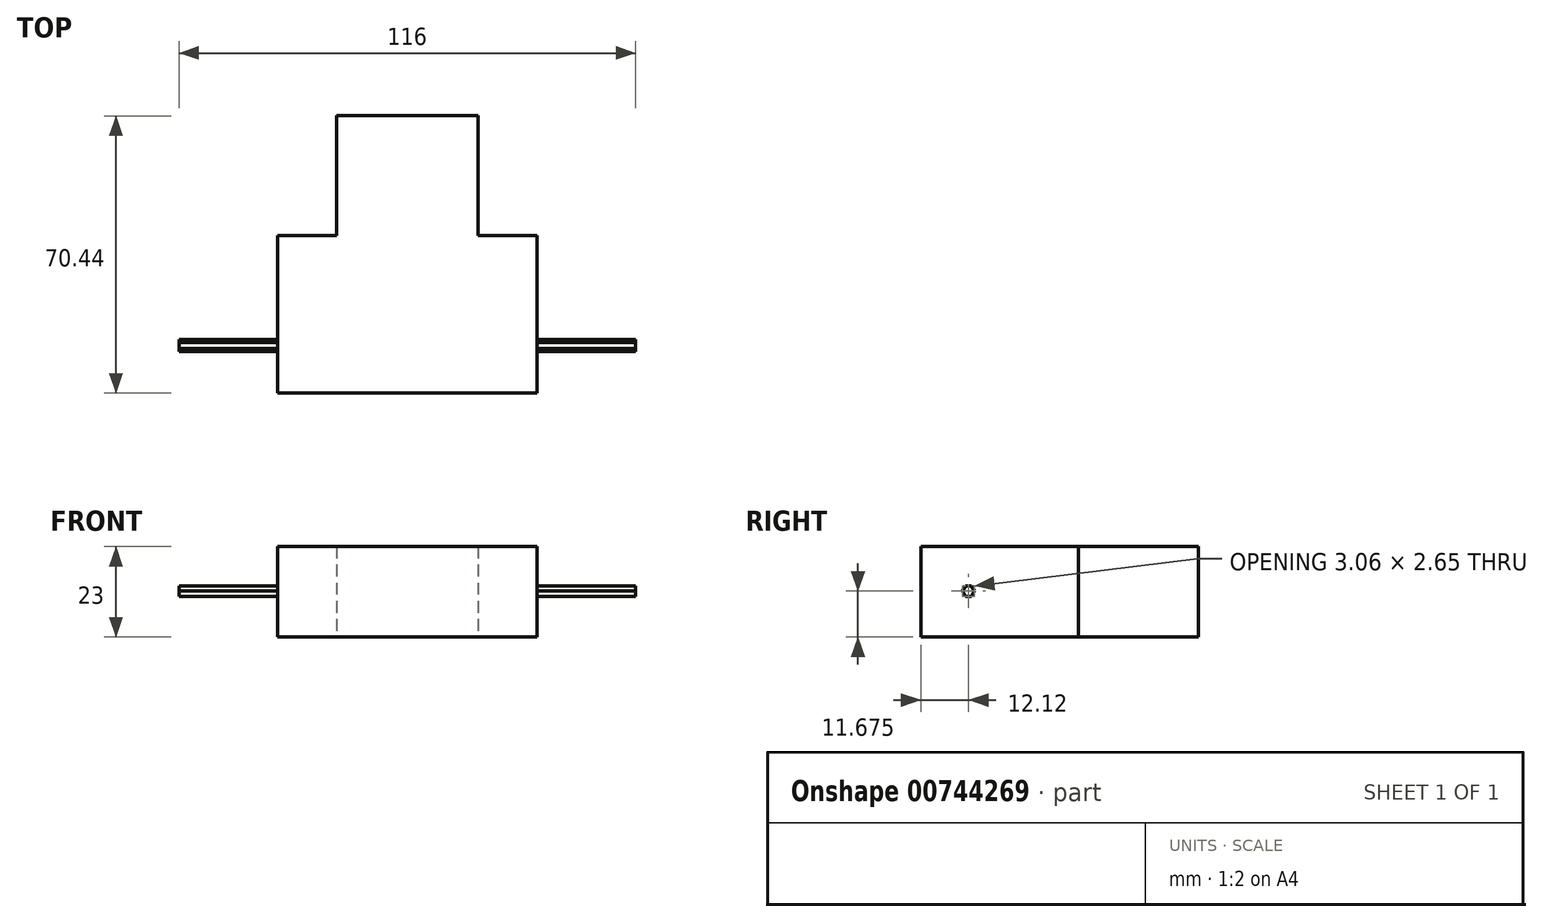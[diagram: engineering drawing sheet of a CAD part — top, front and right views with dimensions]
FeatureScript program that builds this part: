
annotation { "Feature Type Name" : "Feature", "Feature Type Description" : "" }
export const myFeature = defineFeature(function(context is Context, id is Id, definition is map)
    precondition{}
    {
        {
            var Q0;
            Q0=qCreatedBy(makeId("Top.planeOp"),FACE);
            var sketch = newSketch(context, id + "F0", { "sketchPlane" : qUnion([Q0])});
            skLineSegment(sketch, "E0.bottom", {"start": v(-18, 30.44) * mm, "end": v(18, 30.44) * mm});
            skLineSegment(sketch, "E0.top", {"start": v(-18, 0) * mm, "end": v(18, 0) * mm});
            skLineSegment(sketch, "E0.left", {"start": v(-18, 30.44) * mm, "end": v(-18, 0) * mm});
            skLineSegment(sketch, "E0.right", {"start": v(18, 30.44) * mm, "end": v(18, 0) * mm});
            skLineSegment(sketch, "E1.bottom", {"start": v(-33, 0) * mm, "end": v(33, 0) * mm});
            skLineSegment(sketch, "E1.top", {"start": v(-33, -40) * mm, "end": v(33, -40) * mm});
            skLineSegment(sketch, "E1.left", {"start": v(-33, 0) * mm, "end": v(-33, -40) * mm});
            skLineSegment(sketch, "E1.right", {"start": v(33, 0) * mm, "end": v(33, -40) * mm});
            skSolve(sketch);
        }
        {
            var Q0;
            Q0 = qSketchRegion(id + "F0", true);
            extrude(context, id + "F1", {"entities" : qUnion([Q0]), "depth" : 23 * mm, "offsetDistance" : 25 * mm});
        }
        {
            var Q0;
            Q0=makeQuery(id+"F1.opExtrude","SWEPT_FACE",FACE,{"disambiguationData":[OSD([sQuery(id+"F0.wireOp",EDGE,"E1.right")])]});
            var sketch = newSketch(context, id + "F2", { "sketchPlane" : qUnion([Q0])});
            skCircle(sketch, "E2.cCircle", {"center": v(-27.88, 11.68) * mm, "radius": 1.32 * mm, "construction": true});
            skLineSegment(sketch, "E2.0", {"start": v(-28.64, 13) * mm, "end": v(-27.11, 13) * mm});
            skLineSegment(sketch, "E2.1", {"start": v(-27.11, 13) * mm, "end": v(-26.35, 11.68) * mm});
            skLineSegment(sketch, "E2.2", {"start": v(-26.35, 11.68) * mm, "end": v(-27.11, 10.35) * mm});
            skLineSegment(sketch, "E2.3", {"start": v(-27.11, 10.35) * mm, "end": v(-28.64, 10.35) * mm});
            skLineSegment(sketch, "E2.4", {"start": v(-28.64, 10.35) * mm, "end": v(-29.4, 11.68) * mm});
            skLineSegment(sketch, "E2.5", {"start": v(-29.4, 11.68) * mm, "end": v(-28.64, 13) * mm});
            skPoint(sketch, "E2.0.midPoint", {"position": v(-27.88, 13) * mm});
            skSolve(sketch);
        }
        {
            var Q0;
            Q0=makeQuery(id+"F2.imprint","IMPRINT",FACE,{"disambiguationData":[TD([[makeQuery(id+"F2.imprint","IMPRINT",EDGE,{"derivedFrom":sQuery(id+"F2.wireOp",EDGE,"E2.0")}),-1.0]])]});
            extrude(context, id + "F3", {"entities" : qUnion([Q0]), "operationType" : NewBodyOperationType.ADD, "depth" : 25 * mm, "offsetDistance" : 25 * mm});
        }
        {
            var Q0;
            Q0=makeQuery(id+"F1.opExtrude","SWEPT_FACE",FACE,{"disambiguationData":[OSD([sQuery(id+"F0.wireOp",EDGE,"E1.right")])]});
            var sketch = newSketch(context, id + "F4", { "sketchPlane" : qUnion([Q0])});
            skCircle(sketch, "E3.cCircle", {"center": v(-27.88, 11.68) * mm, "radius": 1.32 * mm, "construction": true});
            skPoint(sketch, "E3.cCircle.centerSnap0", {"position": v(-27.88, 10.35) * mm});
            skLineSegment(sketch, "E3.0", {"start": v(-28.64, 13) * mm, "end": v(-27.11, 13) * mm});
            skLineSegment(sketch, "E3.1", {"start": v(-27.11, 13) * mm, "end": v(-26.35, 11.68) * mm});
            skLineSegment(sketch, "E3.2", {"start": v(-26.35, 11.68) * mm, "end": v(-27.11, 10.35) * mm});
            skLineSegment(sketch, "E3.3", {"start": v(-27.11, 10.35) * mm, "end": v(-28.64, 10.35) * mm});
            skLineSegment(sketch, "E3.4", {"start": v(-28.64, 10.35) * mm, "end": v(-29.4, 11.67) * mm});
            skLineSegment(sketch, "E3.5", {"start": v(-29.4, 11.67) * mm, "end": v(-28.64, 13) * mm});
            skPoint(sketch, "E3.0.midPoint", {"position": v(-27.88, 13) * mm});
            skSolve(sketch);
        }
        {
            var Q0;
            Q0 = qSketchRegion(id + "F4", true);
            extrude(context, id + "F5", {"entities" : qUnion([Q0]), "operationType" : NewBodyOperationType.ADD, "oppositeDirection" : true, "depth" : (66 + 25) * mm, "offsetDistance" : 25 * mm});
        }
    });
